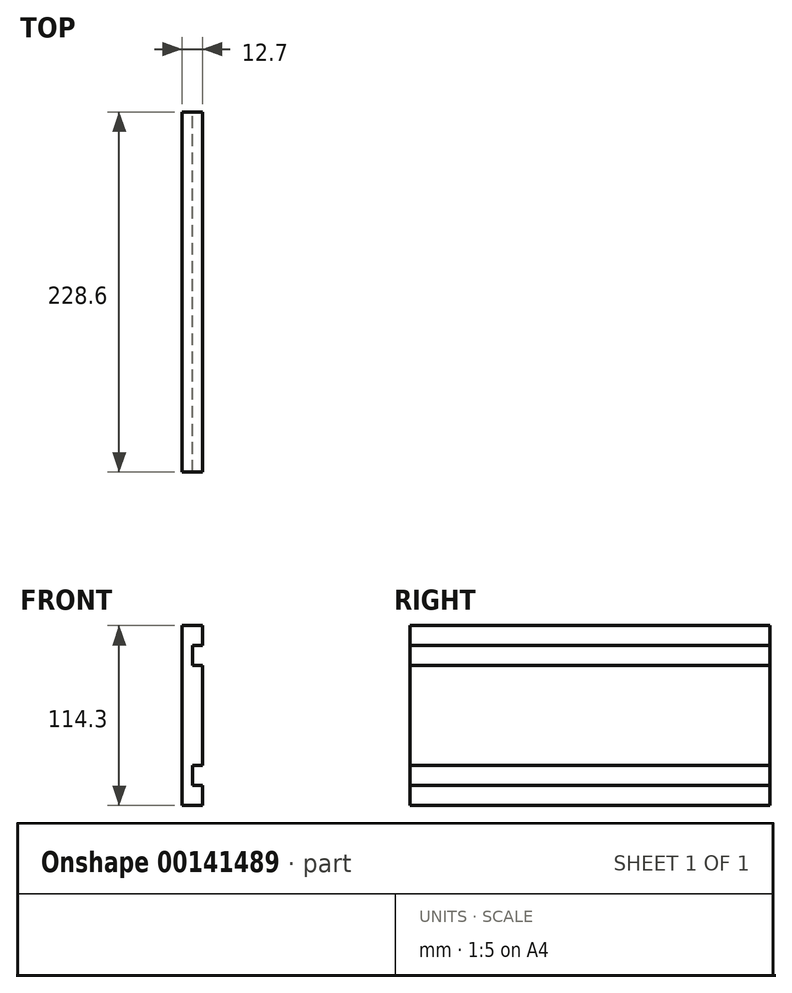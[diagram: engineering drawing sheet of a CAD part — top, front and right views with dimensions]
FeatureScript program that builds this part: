
annotation { "Feature Type Name" : "Feature", "Feature Type Description" : "" }
export const myFeature = defineFeature(function(context is Context, id is Id, definition is map)
    precondition{}
    {
        {
            var Q0;
            Q0=qCreatedBy(makeId("Front.planeOp"),FACE);
            var sketch = newSketch(context, id + "F0", { "sketchPlane" : qUnion([Q0])});
            skLineSegment(sketch, "E0.bottom", {"start": v(0, 114.3) * mm, "end": v(12.7, 114.3) * mm});
            skLineSegment(sketch, "E0.top", {"start": v(0, 0) * mm, "end": v(12.7, 0) * mm});
            skLineSegment(sketch, "E0.left", {"start": v(0, 114.3) * mm, "end": v(0, 0) * mm});
            skLineSegment(sketch, "E0.right", {"start": v(12.7, 114.3) * mm, "end": v(12.7, 101.6) * mm});
            skLineSegment(sketch, "E1.bottom", {"start": v(12.7, 25.4) * mm, "end": v(6.35, 25.4) * mm});
            skLineSegment(sketch, "E1.top", {"start": v(12.7, 12.7) * mm, "end": v(6.35, 12.7) * mm});
            skLineSegment(sketch, "E1.right", {"start": v(6.35, 25.4) * mm, "end": v(6.35, 12.7) * mm});
            skLineSegment(sketch, "E2.trimOffspring", {"start": v(12.7, 12.7) * mm, "end": v(12.7, 0) * mm});
            skLineSegment(sketch, "E3.bottom", {"start": v(12.7, 101.6) * mm, "end": v(6.35, 101.6) * mm});
            skLineSegment(sketch, "E3.top", {"start": v(12.7, 88.9) * mm, "end": v(6.35, 88.9) * mm});
            skLineSegment(sketch, "E3.right", {"start": v(6.35, 101.6) * mm, "end": v(6.35, 88.9) * mm});
            skLineSegment(sketch, "E4.trimOffspring", {"start": v(12.7, 88.9) * mm, "end": v(12.7, 25.4) * mm});
            skSolve(sketch);
        }
        {
            var Q0;
            Q0=makeQuery(id+"F0.imprint","IMPRINT",FACE,{"disambiguationData":[TD([[makeQuery(id+"F0.imprint","IMPRINT",EDGE,{"derivedFrom":sQuery(id+"F0.wireOp",EDGE,"E0.bottom")}),-1.0]])]});
            extrude(context, id + "F1", {"entities" : qUnion([Q0]), "depth" : 228.6 * mm});
        }
    });
